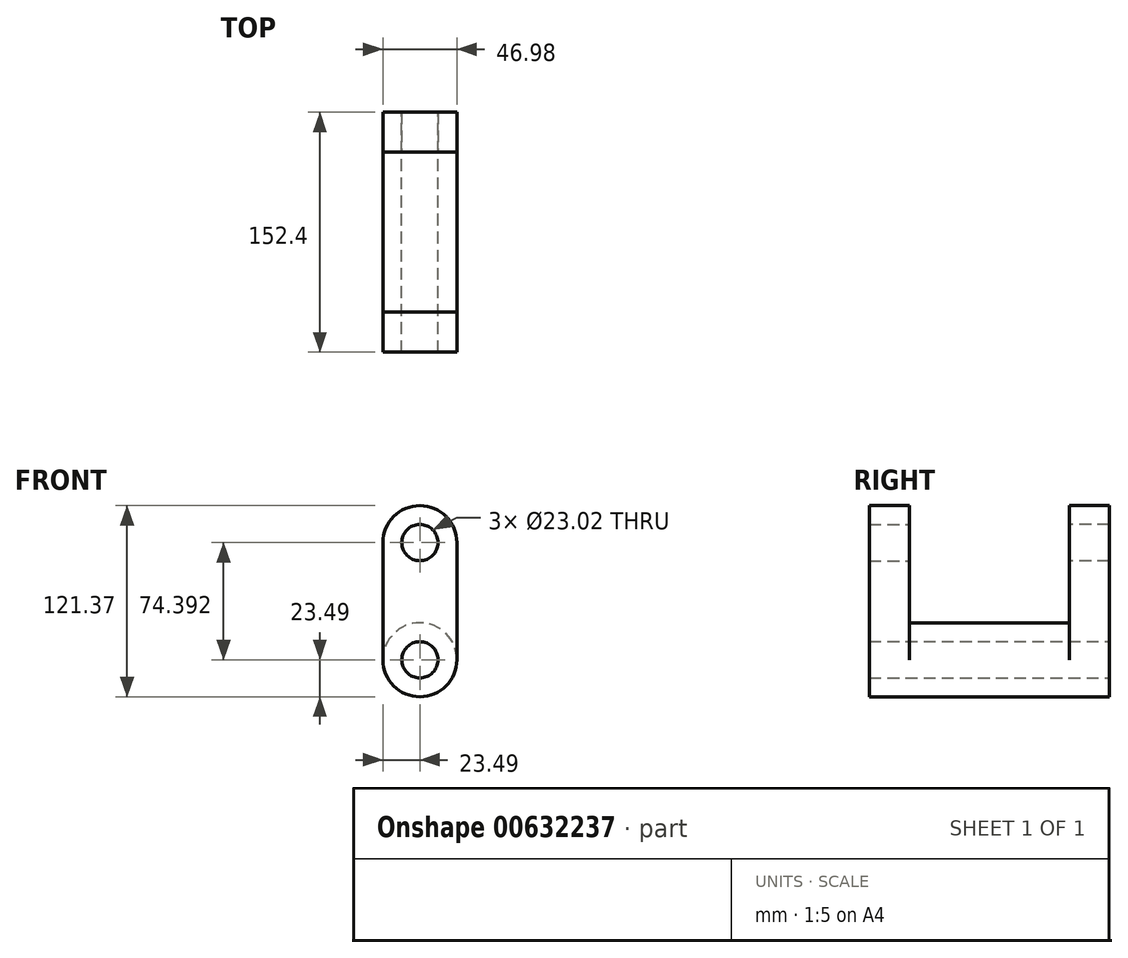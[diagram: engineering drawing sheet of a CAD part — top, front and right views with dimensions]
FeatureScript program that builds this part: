
annotation { "Feature Type Name" : "Feature", "Feature Type Description" : "" }
export const myFeature = defineFeature(function(context is Context, id is Id, definition is map)
    precondition{}
    {
        {
            var Q0;
            Q0=qCreatedBy(makeId("Front.planeOp"),FACE);
            var sketch = newSketch(context, id + "F0", { "sketchPlane" : qUnion([Q0])});
            skCircle(sketch, "E0", {"center": v(0, 0) * mm, "radius": 11.5 * mm});
            skCircle(sketch, "E1", {"center": v(0, 0) * mm, "radius": 23.49 * mm});
            skCircle(sketch, "E2", {"center": v(0, 74.4) * mm, "radius": 11.5 * mm});
            skCircle(sketch, "E3", {"center": v(0, 74.4) * mm, "radius": 23.49 * mm});
            skLineSegment(sketch, "E4", {"start": v(-23.49, 74.4) * mm, "end": v(-23.49, 0) * mm});
            skLineSegment(sketch, "E5", {"start": v(23.49, 74.4) * mm, "end": v(23.49, 0) * mm});
            skSolve(sketch);
        }
        {
            var Q0;
            Q0 = qSketchRegion(id + "F0", true);
            extrude(context, id + "F1", {"entities" : qUnion([Q0]), "depth" : 25.4 * mm, "offsetDistance" : 25.4 * mm});
        }
        {
            var Q0;
            Q0=makeQuery(id+"F0.imprint","IMPRINT",FACE,{"disambiguationData":[TD([[makeQuery(id+"F0.imprint","IMPRINT",EDGE,{"derivedFrom":sQuery(id+"F0.wireOp",EDGE,"E0")}),-1.0]])]});
            extrude(context, id + "F2", {"entities" : qUnion([Q0]), "operationType" : NewBodyOperationType.ADD, "oppositeDirection" : true, "depth" : 50.8 * mm, "offsetDistance" : 25.4 * mm});
        }
        {
            var Q0;
            Q0=makeQuery(id+"F1.opExtrude","SWEPT_BODY",BODY,{"disambiguationData":[OSD([sQuery(id+"F0.wireOp",EDGE,"E0"),sQuery(id+"F0.wireOp",EDGE,"E1"),sQuery(id+"F0.wireOp",EDGE,"E2"),sQuery(id+"F0.wireOp",EDGE,"E3"),sQuery(id+"F0.wireOp",EDGE,"E4"),sQuery(id+"F0.wireOp",EDGE,"E5")])]});
            var Q1;
            Q1=makeQuery(id+"F2.opExtrude","CAP_FACE",FACE,{"disambiguationData":[OSD([sQuery(id+"F0.wireOp",EDGE,"E0"),sQuery(id+"F0.wireOp",EDGE,"E1")])],"isStart":false});
            mirror(context, id + "F3", {"operationType" : NewBodyOperationType.ADD, "entities" : qUnion([Q0]), "mirrorPlane" : qUnion([Q1])});
        }
    });
